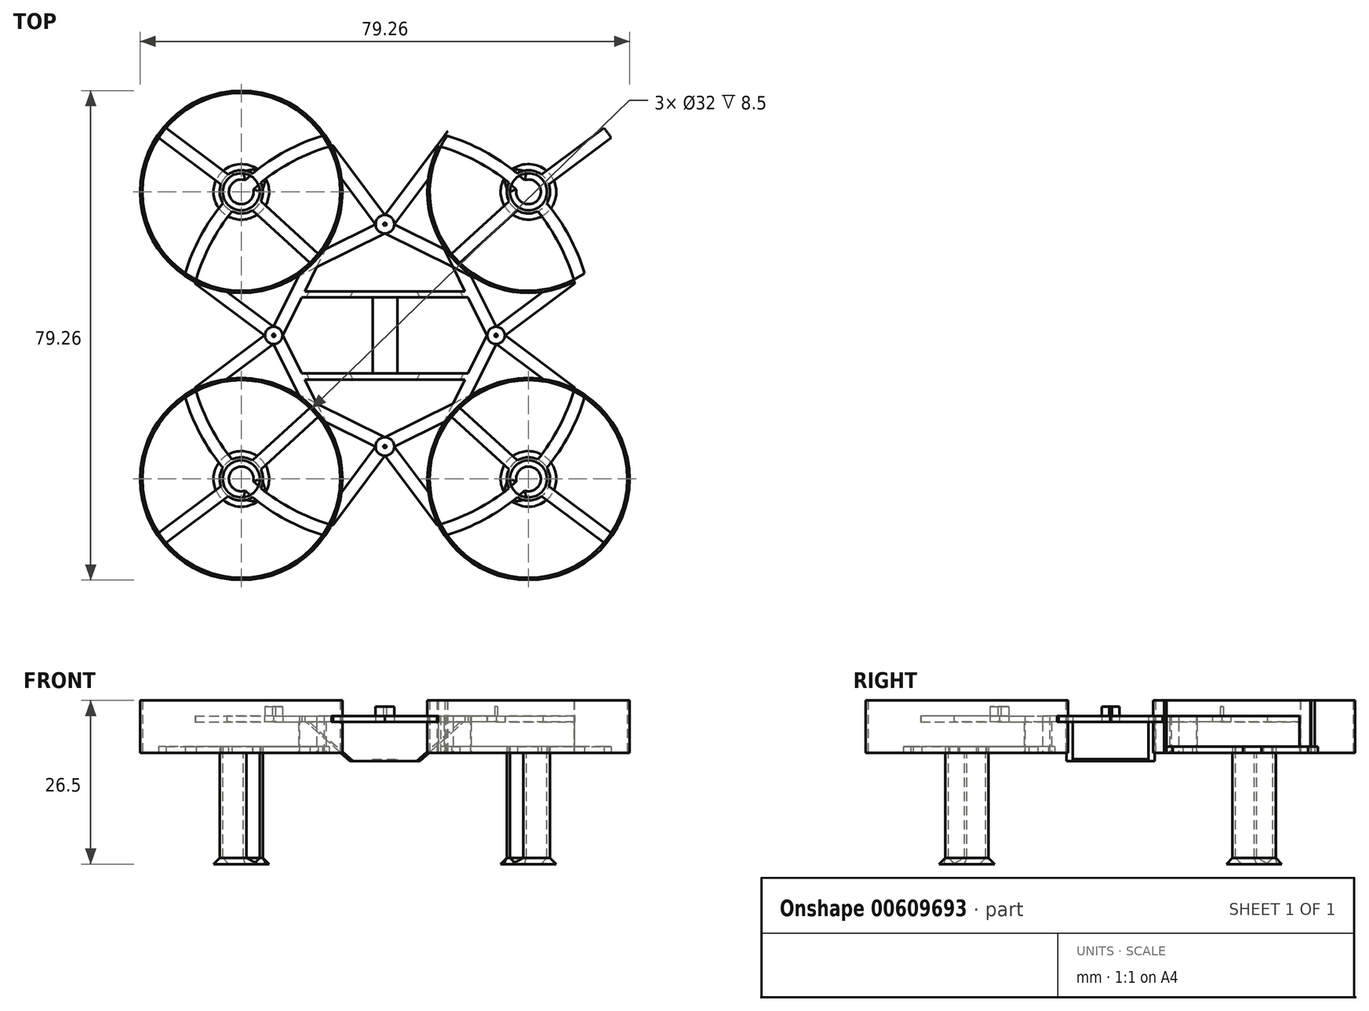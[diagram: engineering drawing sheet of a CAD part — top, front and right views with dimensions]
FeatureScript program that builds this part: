
annotation { "Feature Type Name" : "Feature", "Feature Type Description" : "" }
export const myFeature = defineFeature(function(context is Context, id is Id, definition is map)
    precondition{}
    {
        {
            var Q0;
            Q0=qCreatedBy(makeId("Top.planeOp"),FACE);
            var sketch = newSketch(context, id + "F0", { "sketchPlane" : qUnion([Q0])});
            skCircle(sketch, "E0", {"center": v(-23.25, 23.25) * mm, "radius": 16 * mm});
            skCircle(sketch, "E1", {"center": v(-23.25, -23.25) * mm, "radius": 16 * mm});
            skCircle(sketch, "E2", {"center": v(-18, 0) * mm, "radius": 0.25 * mm});
            skCircle(sketch, "E3", {"center": v(0, -18) * mm, "radius": 0.25 * mm});
            skCircle(sketch, "E4", {"center": v(-23.25, -23.25) * mm, "radius": 16.38 * mm});
            skCircle(sketch, "E5", {"center": v(-23.25, 23.25) * mm, "radius": 16.38 * mm});
            skCircle(sketch, "E6", {"center": v(-23.25, 23.25) * mm, "radius": 3.5 * mm});
            skCircle(sketch, "E7", {"center": v(-23.25, 23.25) * mm, "radius": 3 * mm});
            skCircle(sketch, "E8.0", {"center": v(0, 0) * mm, "radius": 33.88 * mm});
            skCircle(sketch, "E9.0", {"center": v(0, 0) * mm, "radius": 31.88 * mm});
            skCircle(sketch, "E10.MirrorC", {"center": v(-23.25, -23.25) * mm, "radius": 3.5 * mm});
            skCircle(sketch, "E11.MirrorC", {"center": v(-23.25, -23.25) * mm, "radius": 3 * mm});
            skLineSegment(sketch, "E12", {"start": v(-16.5, 0) * mm, "end": v(-8.58, -15.98) * mm});
            skLineSegment(sketch, "E13.MirrorCS", {"start": v(-16.5, 0) * mm, "end": v(-8.58, 15.98) * mm});
            skLineSegment(sketch, "E14", {"start": v(-33.06, -10.14) * mm, "end": v(-19.5, 0) * mm});
            skLineSegment(sketch, "E15", {"start": v(-18.04, -1.4) * mm, "end": v(-25.58, -7.04) * mm});
            skLineSegment(sketch, "E16.MirrorCS", {"start": v(-33.06, 10.14) * mm, "end": v(-19.5, 0) * mm});
            skLineSegment(sketch, "E17.MirrorCS", {"start": v(-18.04, 1.4) * mm, "end": v(-25.58, 7.04) * mm});
            skLineSegment(sketch, "E18.trimOffspring", {"start": v(-18.04, 1.4) * mm, "end": v(-13.85, 9.84) * mm});
            skLineSegment(sketch, "E19.trimOffspring", {"start": v(-18.04, -1.4) * mm, "end": v(-13.85, -9.84) * mm});
            skCircle(sketch, "E20.MirrorC", {"center": v(23.25, 23.25) * mm, "radius": 3 * mm});
            skCircle(sketch, "E21.MirrorC", {"center": v(23.25, 23.25) * mm, "radius": 3.5 * mm});
            skCircle(sketch, "E22.MirrorC", {"center": v(23.25, 23.25) * mm, "radius": 16 * mm});
            skCircle(sketch, "E23.MirrorC", {"center": v(23.25, 23.25) * mm, "radius": 16.38 * mm});
            skLineSegment(sketch, "E24.MirrorCS", {"start": v(16.5, 0) * mm, "end": v(8.58, 15.98) * mm});
            skLineSegment(sketch, "E25.MirrorCS", {"start": v(18.04, 1.4) * mm, "end": v(13.85, 9.84) * mm});
            skLineSegment(sketch, "E26.MirrorCS", {"start": v(18.04, 1.4) * mm, "end": v(25.58, 7.04) * mm});
            skLineSegment(sketch, "E27.MirrorCS", {"start": v(33.06, 10.14) * mm, "end": v(19.5, 0) * mm});
            skLineSegment(sketch, "E28.MirrorCS", {"start": v(33.06, -10.14) * mm, "end": v(19.5, 0) * mm});
            skLineSegment(sketch, "E29.MirrorCS", {"start": v(18.04, -1.4) * mm, "end": v(25.58, -7.04) * mm});
            skLineSegment(sketch, "E30.MirrorCS", {"start": v(18.04, -1.4) * mm, "end": v(13.85, -9.84) * mm});
            skLineSegment(sketch, "E31.MirrorCS", {"start": v(16.5, 0) * mm, "end": v(8.58, -15.98) * mm});
            skCircle(sketch, "E32.MirrorC", {"center": v(23.25, -23.25) * mm, "radius": 16.38 * mm});
            skCircle(sketch, "E33.MirrorC", {"center": v(23.25, -23.25) * mm, "radius": 16 * mm});
            skCircle(sketch, "E34.MirrorC", {"center": v(23.25, -23.25) * mm, "radius": 3 * mm});
            skCircle(sketch, "E35.MirrorC", {"center": v(23.25, -23.25) * mm, "radius": 3.5 * mm});
            skLineSegment(sketch, "E36", {"start": v(0, -16.5) * mm, "end": v(15.98, -8.58) * mm});
            skLineSegment(sketch, "E37", {"start": v(0, -16.5) * mm, "end": v(-15.98, -8.58) * mm});
            skLineSegment(sketch, "E38", {"start": v(-10.14, -33.06) * mm, "end": v(0, -19.5) * mm});
            skLineSegment(sketch, "E39", {"start": v(-1.5, -18) * mm, "end": v(-7.01, -25.37) * mm});
            skLineSegment(sketch, "E40", {"start": v(1.5, -18) * mm, "end": v(7.01, -25.37) * mm});
            skLineSegment(sketch, "E41.trimOffspring", {"start": v(-1.5, -18) * mm, "end": v(-9.83, -13.87) * mm});
            skLineSegment(sketch, "E42.trimOffspring", {"start": v(1.5, -18) * mm, "end": v(9.83, -13.87) * mm});
            skLineSegment(sketch, "E43", {"start": v(0, -19.5) * mm, "end": v(10.14, -33.06) * mm});
            skLineSegment(sketch, "E44.MirrorCS", {"start": v(0, 16.5) * mm, "end": v(15.98, 8.58) * mm});
            skLineSegment(sketch, "E45.MirrorCS", {"start": v(1.5, 18) * mm, "end": v(9.83, 13.87) * mm});
            skLineSegment(sketch, "E46.MirrorCS", {"start": v(1.5, 18) * mm, "end": v(7.01, 25.37) * mm});
            skLineSegment(sketch, "E47.MirrorCS", {"start": v(0, 19.5) * mm, "end": v(10.14, 33.06) * mm});
            skLineSegment(sketch, "E48.MirrorCS", {"start": v(-10.14, 33.06) * mm, "end": v(0, 19.5) * mm});
            skLineSegment(sketch, "E49.MirrorCS", {"start": v(-1.5, 18) * mm, "end": v(-7.01, 25.37) * mm});
            skLineSegment(sketch, "E50.MirrorCS", {"start": v(-1.5, 18) * mm, "end": v(-9.83, 13.87) * mm});
            skLineSegment(sketch, "E51.MirrorCS", {"start": v(0, 16.5) * mm, "end": v(-15.98, 8.58) * mm});
            skCircle(sketch, "E52.MirrorC", {"center": v(0, 18) * mm, "radius": 0.25 * mm});
            skLineSegment(sketch, "E53", {"start": v(-13.45, 6.15) * mm, "end": v(13.45, 6.15) * mm});
            skLineSegment(sketch, "E54", {"start": v(-13.45, -6.15) * mm, "end": v(13.45, -6.15) * mm});
            skLineSegment(sketch, "E55.0", {"start": v(-12.96, 7.15) * mm, "end": v(12.96, 7.15) * mm});
            skLineSegment(sketch, "E56.MirrorCS", {"start": v(-12.96, -7.15) * mm, "end": v(12.96, -7.15) * mm});
            skLineSegment(sketch, "E57", {"start": v(-2, 6.15) * mm, "end": v(-2, -6.15) * mm});
            skLineSegment(sketch, "E58.MirrorCS", {"start": v(2, 6.15) * mm, "end": v(2, -6.15) * mm});
            skLineSegment(sketch, "E59", {"start": v(-35.46, 33.58) * mm, "end": v(-25.34, 26.05) * mm});
            skLineSegment(sketch, "E60", {"start": v(-26.54, 24.45) * mm, "end": v(-36.66, 31.98) * mm});
            skLineSegment(sketch, "E61.MirrorCS", {"start": v(-26.54, -24.45) * mm, "end": v(-36.66, -31.98) * mm});
            skLineSegment(sketch, "E62.MirrorCS", {"start": v(-35.46, -33.58) * mm, "end": v(-25.34, -26.05) * mm});
            skLineSegment(sketch, "E63.MirrorCS", {"start": v(35.46, 33.58) * mm, "end": v(25.34, 26.05) * mm});
            skLineSegment(sketch, "E64.MirrorCS", {"start": v(26.54, 24.45) * mm, "end": v(36.66, 31.98) * mm});
            skLineSegment(sketch, "E65.MirrorCS", {"start": v(26.54, -24.45) * mm, "end": v(36.66, -31.98) * mm});
            skLineSegment(sketch, "E66.MirrorCS", {"start": v(35.46, -33.58) * mm, "end": v(25.34, -26.05) * mm});
            skLineSegment(sketch, "E67", {"start": v(20.1, 21.73) * mm, "end": v(10.78, 13.22) * mm});
            skLineSegment(sketch, "E68", {"start": v(21.45, 20.25) * mm, "end": v(12.13, 11.74) * mm});
            skLineSegment(sketch, "E69.MirrorCS", {"start": v(21.45, -20.25) * mm, "end": v(12.13, -11.74) * mm});
            skLineSegment(sketch, "E70.MirrorCS", {"start": v(20.1, -21.73) * mm, "end": v(10.78, -13.22) * mm});
            skLineSegment(sketch, "E71.MirrorCS", {"start": v(-20.1, 21.73) * mm, "end": v(-10.78, 13.22) * mm});
            skLineSegment(sketch, "E72.MirrorCS", {"start": v(-21.45, 20.25) * mm, "end": v(-12.13, 11.74) * mm});
            skLineSegment(sketch, "E73.MirrorCS", {"start": v(-21.45, -20.25) * mm, "end": v(-12.13, -11.74) * mm});
            skLineSegment(sketch, "E74.MirrorCS", {"start": v(-20.1, -21.73) * mm, "end": v(-10.78, -13.22) * mm});
            skCircle(sketch, "E75.MirrorC", {"center": v(18, 0) * mm, "radius": 0.25 * mm});
            skCircle(sketch, "E76", {"center": v(-18, 0) * mm, "radius": 1.4 * mm});
            skCircle(sketch, "E77", {"center": v(0, 18) * mm, "radius": 1.5 * mm});
            skCircle(sketch, "E78", {"center": v(18, 0) * mm, "radius": 1.4 * mm});
            skCircle(sketch, "E79", {"center": v(0, -18) * mm, "radius": 1.5 * mm});
            skLineSegment(sketch, "E80", {"start": v(-22.92, 26.23) * mm, "end": v(-22.44, 26.66) * mm});
            skLineSegment(sketch, "E81", {"start": v(-20.25, 23.25) * mm, "end": v(-19.78, 23.67) * mm});
            skLineSegment(sketch, "E82.MirrorCS", {"start": v(22.92, 26.23) * mm, "end": v(22.44, 26.66) * mm});
            skLineSegment(sketch, "E83.MirrorCS", {"start": v(20.25, 23.25) * mm, "end": v(19.78, 23.67) * mm});
            skLineSegment(sketch, "E84.MirrorCS", {"start": v(20.25, -23.25) * mm, "end": v(19.78, -23.67) * mm});
            skLineSegment(sketch, "E85.MirrorCS", {"start": v(22.92, -26.23) * mm, "end": v(22.44, -26.66) * mm});
            skLineSegment(sketch, "E86.MirrorCS", {"start": v(-20.25, -23.25) * mm, "end": v(-19.78, -23.67) * mm});
            skLineSegment(sketch, "E87.MirrorCS", {"start": v(-22.92, -26.23) * mm, "end": v(-22.44, -26.66) * mm});
            skSolve(sketch);
        }
        {
            var Q0;
            {var subQ0=sQuery(id+"F0.wireOp",EDGE,"E32.MirrorC");var subQ3=sQuery(id+"F0.wireOp",EDGE,"E8.0");var subQ5=makeQuery(id+"F0.imprint","INTERSECT",VERTEX,{"disambiguationData":[OD(0.0)],"derivedFrom":[subQ3,subQ0]});Q0=makeQuery(id+"F0.imprint","IMPRINT",FACE,{"disambiguationData":[TD([[makeQuery(id+"F0.imprint","IMPRINT",EDGE,{"disambiguationData":[TD([[subQ5,-1.0]])],"derivedFrom":subQ3}),-1.0]])]});}
            var Q1;
            {var subQ0=sQuery(id+"F0.wireOp",EDGE,"E32.MirrorC");var subQ1=sQuery(id+"F0.wireOp",EDGE,"E8.0");var subQ2=makeQuery(id+"F0.imprint","INTERSECT",VERTEX,{"disambiguationData":[OD(0.0)],"derivedFrom":[subQ1,subQ0]});Q1=makeQuery(id+"F0.imprint","IMPRINT",FACE,{"disambiguationData":[TD([[makeQuery(id+"F0.imprint","IMPRINT",EDGE,{"disambiguationData":[TD([[subQ2,-1.0]])],"derivedFrom":subQ1}),1.0]])]});}
            var Q2;
            {var subQ0=sQuery(id+"F0.wireOp",EDGE,"E32.MirrorC");var subQ2=sQuery(id+"F0.wireOp",EDGE,"E9.0");var subQ3=makeQuery(id+"F0.imprint","INTERSECT",VERTEX,{"disambiguationData":[OD(0.0)],"derivedFrom":[subQ2,subQ0]});Q2=makeQuery(id+"F0.imprint","IMPRINT",FACE,{"disambiguationData":[TD([[makeQuery(id+"F0.imprint","IMPRINT",EDGE,{"disambiguationData":[TD([[subQ3,-1.0]])],"derivedFrom":subQ2}),1.0]])]});}
            var Q3;
            {var subQ0=sQuery(id+"F0.wireOp",EDGE,"E33.MirrorC");var subQ1=sQuery(id+"F0.wireOp",EDGE,"E8.0");var subQ2=makeQuery(id+"F0.imprint","INTERSECT",VERTEX,{"disambiguationData":[OD(1.0)],"derivedFrom":[subQ1,subQ0]});Q3=makeQuery(id+"F0.imprint","IMPRINT",FACE,{"disambiguationData":[TD([[makeQuery(id+"F0.imprint","IMPRINT",EDGE,{"disambiguationData":[TD([[subQ2,-1.0]])],"derivedFrom":subQ1}),1.0]])]});}
            extrude(context, id + "F1", {"entities" : qUnion([Q0, Q1, Q2, Q3]), "depth" : 8.5 * mm, "offsetDistance" : 25 * mm});
        }
        {
            var Q0;
            {var subQ0=sQuery(id+"F0.wireOp",EDGE,"E23.MirrorC");var subQ4=sQuery(id+"F0.wireOp",EDGE,"E9.0");var subQ9=makeQuery(id+"F0.imprint","INTERSECT",VERTEX,{"disambiguationData":[OD(0.0)],"derivedFrom":[subQ4,subQ0]});Q0=makeQuery(id+"F0.imprint","IMPRINT",FACE,{"disambiguationData":[TD([[makeQuery(id+"F0.imprint","IMPRINT",EDGE,{"disambiguationData":[TD([[subQ9,-1.0]])],"derivedFrom":subQ4}),1.0]])]});}
            var Q1;
            {var subQ3=sQuery(id+"F0.wireOp",EDGE,"E8.0");var subQ5=sQuery(id+"F0.wireOp",EDGE,"E23.MirrorC");var subQ8=makeQuery(id+"F0.imprint","INTERSECT",VERTEX,{"disambiguationData":[OD(0.0)],"derivedFrom":[subQ3,subQ5]});Q1=makeQuery(id+"F0.imprint","IMPRINT",FACE,{"disambiguationData":[TD([[makeQuery(id+"F0.imprint","IMPRINT",EDGE,{"disambiguationData":[TD([[subQ8,-1.0]])],"derivedFrom":subQ3}),-1.0]])]});}
            var Q2;
            {var subQ0=sQuery(id+"F0.wireOp",EDGE,"E22.MirrorC");var subQ1=sQuery(id+"F0.wireOp",EDGE,"E8.0");var subQ2=makeQuery(id+"F0.imprint","INTERSECT",VERTEX,{"disambiguationData":[OD(1.0)],"derivedFrom":[subQ1,subQ0]});Q2=makeQuery(id+"F0.imprint","IMPRINT",FACE,{"disambiguationData":[TD([[makeQuery(id+"F0.imprint","IMPRINT",EDGE,{"disambiguationData":[TD([[subQ2,-1.0]])],"derivedFrom":subQ1}),1.0]])]});}
            var Q3;
            {var subQ0=sQuery(id+"F0.wireOp",EDGE,"E23.MirrorC");var subQ1=sQuery(id+"F0.wireOp",EDGE,"E8.0");var subQ2=makeQuery(id+"F0.imprint","INTERSECT",VERTEX,{"disambiguationData":[OD(0.0)],"derivedFrom":[subQ1,subQ0]});Q3=makeQuery(id+"F0.imprint","IMPRINT",FACE,{"disambiguationData":[TD([[makeQuery(id+"F0.imprint","IMPRINT",EDGE,{"disambiguationData":[TD([[subQ2,-1.0]])],"derivedFrom":subQ1}),1.0]])]});}
            var Q4;
            {var subQ5=sQuery(id+"F0.wireOp",EDGE,"E0");var subQ9=makeQuery(id+"F0.imprint","INTERSECT",VERTEX,{"derivedFrom":[subQ5,sQuery(id+"F0.wireOp",EDGE,"E72.MirrorCS")]});Q4=makeQuery(id+"F0.imprint","IMPRINT",FACE,{"disambiguationData":[TD([[makeQuery(id+"F0.imprint","IMPRINT",EDGE,{"disambiguationData":[TD([[subQ9,1.0]])],"derivedFrom":subQ5}),-1.0]])]});}
            var Q5;
            {var subQ0=sQuery(id+"F0.wireOp",EDGE,"E8.0");var subQ1=sQuery(id+"F0.wireOp",EDGE,"E0");var subQ2=makeQuery(id+"F0.imprint","INTERSECT",VERTEX,{"disambiguationData":[OD(0.0)],"derivedFrom":[subQ1,subQ0]});Q5=makeQuery(id+"F0.imprint","IMPRINT",FACE,{"disambiguationData":[TD([[makeQuery(id+"F0.imprint","IMPRINT",EDGE,{"disambiguationData":[TD([[subQ2,1.0]])],"derivedFrom":subQ1}),-1.0]])]});}
            var Q6;
            {var subQ0=sQuery(id+"F0.wireOp",EDGE,"E0");var subQ8=makeQuery(id+"F0.imprint","INTERSECT",VERTEX,{"derivedFrom":[subQ0,sQuery(id+"F0.wireOp",EDGE,"E59")]});Q6=makeQuery(id+"F0.imprint","IMPRINT",FACE,{"disambiguationData":[TD([[makeQuery(id+"F0.imprint","IMPRINT",EDGE,{"disambiguationData":[TD([[subQ8,1.0]])],"derivedFrom":subQ0}),-1.0]])]});}
            var Q7;
            {var subQ0=sQuery(id+"F0.wireOp",EDGE,"E8.0");var subQ1=sQuery(id+"F0.wireOp",EDGE,"E0");var subQ2=makeQuery(id+"F0.imprint","INTERSECT",VERTEX,{"disambiguationData":[OD(1.0)],"derivedFrom":[subQ1,subQ0]});Q7=makeQuery(id+"F0.imprint","IMPRINT",FACE,{"disambiguationData":[TD([[makeQuery(id+"F0.imprint","IMPRINT",EDGE,{"disambiguationData":[TD([[subQ2,-1.0]])],"derivedFrom":subQ1}),-1.0]])]});}
            var Q8;
            {var subQ4=sQuery(id+"F0.wireOp",EDGE,"E1");var subQ7=makeQuery(id+"F0.imprint","INTERSECT",VERTEX,{"derivedFrom":[subQ4,sQuery(id+"F0.wireOp",EDGE,"E61.MirrorCS")]});Q8=makeQuery(id+"F0.imprint","IMPRINT",FACE,{"disambiguationData":[TD([[makeQuery(id+"F0.imprint","IMPRINT",EDGE,{"disambiguationData":[TD([[subQ7,1.0]])],"derivedFrom":subQ4}),-1.0]])]});}
            var Q9;
            {var subQ0=sQuery(id+"F0.wireOp",EDGE,"E8.0");var subQ1=sQuery(id+"F0.wireOp",EDGE,"E1");var subQ2=makeQuery(id+"F0.imprint","INTERSECT",VERTEX,{"disambiguationData":[OD(1.0)],"derivedFrom":[subQ1,subQ0]});Q9=makeQuery(id+"F0.imprint","IMPRINT",FACE,{"disambiguationData":[TD([[makeQuery(id+"F0.imprint","IMPRINT",EDGE,{"disambiguationData":[TD([[subQ2,-1.0]])],"derivedFrom":subQ1}),-1.0]])]});}
            var Q10;
            {var subQ9=sQuery(id+"F0.wireOp",EDGE,"E1");var subQ10=makeQuery(id+"F0.imprint","INTERSECT",VERTEX,{"derivedFrom":[subQ9,sQuery(id+"F0.wireOp",EDGE,"E73.MirrorCS")]});Q10=makeQuery(id+"F0.imprint","IMPRINT",FACE,{"disambiguationData":[TD([[makeQuery(id+"F0.imprint","IMPRINT",EDGE,{"disambiguationData":[TD([[subQ10,1.0]])],"derivedFrom":subQ9}),-1.0]])]});}
            var Q11;
            {var subQ0=sQuery(id+"F0.wireOp",EDGE,"E9.0");var subQ1=sQuery(id+"F0.wireOp",EDGE,"E1");var subQ2=makeQuery(id+"F0.imprint","INTERSECT",VERTEX,{"disambiguationData":[OD(0.0)],"derivedFrom":[subQ1,subQ0]});Q11=makeQuery(id+"F0.imprint","IMPRINT",FACE,{"disambiguationData":[TD([[makeQuery(id+"F0.imprint","IMPRINT",EDGE,{"disambiguationData":[TD([[subQ2,-1.0]])],"derivedFrom":subQ1}),-1.0]])]});}
            extrude(context, id + "F2", {"entities" : qUnion([Q0, Q1, Q2, Q3, Q4, Q5, Q6, Q7, Q8, Q9, Q10, Q11]), "depth" : 8.5 * mm, "offsetDistance" : 25 * mm});
        }
        {
            var Q0;
            {var subQ0=sQuery(id+"F0.wireOp",EDGE,"E46.MirrorCS");Q0=makeQuery(id+"F0.imprint","IMPRINT",FACE,{"disambiguationData":[TD([[makeQuery(id+"F0.imprint","IMPRINT",EDGE,{"derivedFrom":subQ0}),1.0]])]});}
            var Q1;
            {var subQ5=sQuery(id+"F0.wireOp",EDGE,"E26.MirrorCS");Q1=makeQuery(id+"F0.imprint","IMPRINT",FACE,{"disambiguationData":[TD([[makeQuery(id+"F0.imprint","IMPRINT",EDGE,{"derivedFrom":subQ5}),-1.0]])]});}
            var Q2;
            Q2=makeQuery(id+"F0.imprint","IMPRINT",FACE,{"disambiguationData":[TD([[makeQuery(id+"F0.imprint","IMPRINT",EDGE,{"derivedFrom":sQuery(id+"F0.wireOp",EDGE,"E3")}),-1.0]])]});
            var Q3;
            Q3=makeQuery(id+"F0.imprint","IMPRINT",FACE,{"disambiguationData":[TD([[makeQuery(id+"F0.imprint","IMPRINT",EDGE,{"derivedFrom":sQuery(id+"F0.wireOp",EDGE,"E2")}),-1.0]])]});
            var Q4;
            {var subQ3=sQuery(id+"F0.wireOp",EDGE,"E19.trimOffspring");var subQ5=sQuery(id+"F0.wireOp",EDGE,"E4");var subQ6=makeQuery(id+"F0.imprint","INTERSECT",VERTEX,{"derivedFrom":[subQ5,subQ3]});Q4=makeQuery(id+"F0.imprint","IMPRINT",FACE,{"disambiguationData":[TD([[makeQuery(id+"F0.imprint","IMPRINT",EDGE,{"disambiguationData":[TD([[subQ6,1.0]])],"derivedFrom":subQ5}),-1.0]])]});}
            var Q5;
            {var subQ0=sQuery(id+"F0.wireOp",EDGE,"E32.MirrorC");var subQ1=sQuery(id+"F0.wireOp",EDGE,"E30.MirrorCS");var subQ2=makeQuery(id+"F0.imprint","INTERSECT",VERTEX,{"derivedFrom":[subQ1,subQ0]});Q5=makeQuery(id+"F0.imprint","IMPRINT",FACE,{"disambiguationData":[TD([[makeQuery(id+"F0.imprint","IMPRINT",EDGE,{"disambiguationData":[TD([[subQ2,1.0]])],"derivedFrom":subQ1}),-1.0]])]});}
            var Q6;
            {var subQ0=sQuery(id+"F0.wireOp",EDGE,"E25.MirrorCS");var subQ1=sQuery(id+"F0.wireOp",EDGE,"E23.MirrorC");var subQ2=makeQuery(id+"F0.imprint","INTERSECT",VERTEX,{"derivedFrom":[subQ1,subQ0]});Q6=makeQuery(id+"F0.imprint","IMPRINT",FACE,{"disambiguationData":[TD([[makeQuery(id+"F0.imprint","IMPRINT",EDGE,{"disambiguationData":[TD([[subQ2,-1.0]])],"derivedFrom":subQ1}),1.0]])]});}
            var Q7;
            {var subQ1=sQuery(id+"F0.wireOp",EDGE,"E5");var subQ5=sQuery(id+"F0.wireOp",EDGE,"E18.trimOffspring");var subQ6=makeQuery(id+"F0.imprint","INTERSECT",VERTEX,{"derivedFrom":[subQ1,subQ5]});Q7=makeQuery(id+"F0.imprint","IMPRINT",FACE,{"disambiguationData":[TD([[makeQuery(id+"F0.imprint","IMPRINT",EDGE,{"disambiguationData":[TD([[subQ6,-1.0]])],"derivedFrom":subQ1}),-1.0]])]});}
            var Q8;
            {var subQ5=sQuery(id+"F0.wireOp",EDGE,"E56.MirrorCS");Q8=makeQuery(id+"F0.imprint","IMPRINT",FACE,{"disambiguationData":[TD([[makeQuery(id+"F0.imprint","IMPRINT",EDGE,{"derivedFrom":subQ5}),1.0]])]});}
            var Q9;
            {var subQ6=sQuery(id+"F0.wireOp",EDGE,"E55.0");Q9=makeQuery(id+"F0.imprint","IMPRINT",FACE,{"disambiguationData":[TD([[makeQuery(id+"F0.imprint","IMPRINT",EDGE,{"derivedFrom":subQ6}),-1.0]])]});}
            var Q10;
            {var subQ1=sQuery(id+"F0.wireOp",EDGE,"E13.MirrorCS");var subQ10=sQuery(id+"F0.wireOp",EDGE,"E12");var subQ15=makeQuery(id+"F0.imprint","INTERSECT",VERTEX,{"derivedFrom":[subQ10,subQ1]});Q10=makeQuery(id+"F0.imprint","IMPRINT",FACE,{"disambiguationData":[TD([[makeQuery(id+"F0.imprint","IMPRINT",EDGE,{"disambiguationData":[TD([[subQ15,-1.0]])],"derivedFrom":subQ10}),-1.0]])]});}
            var Q11;
            {var subQ11=sQuery(id+"F0.wireOp",EDGE,"E15");Q11=makeQuery(id+"F0.imprint","IMPRINT",FACE,{"disambiguationData":[TD([[makeQuery(id+"F0.imprint","IMPRINT",EDGE,{"derivedFrom":subQ11}),-1.0]])]});}
            var Q12;
            {var subQ0=sQuery(id+"F0.wireOp",EDGE,"E37");var subQ1=sQuery(id+"F0.wireOp",EDGE,"E12");var subQ2=makeQuery(id+"F0.imprint","INTERSECT",VERTEX,{"derivedFrom":[subQ1,subQ0]});Q12=makeQuery(id+"F0.imprint","IMPRINT",FACE,{"disambiguationData":[TD([[makeQuery(id+"F0.imprint","IMPRINT",EDGE,{"disambiguationData":[TD([[subQ2,-1.0]])],"derivedFrom":subQ1}),1.0]])]});}
            var Q13;
            {var subQ5=sQuery(id+"F0.wireOp",EDGE,"E39");Q13=makeQuery(id+"F0.imprint","IMPRINT",FACE,{"disambiguationData":[TD([[makeQuery(id+"F0.imprint","IMPRINT",EDGE,{"derivedFrom":subQ5}),1.0]])]});}
            var Q14;
            {var subQ0=sQuery(id+"F0.wireOp",EDGE,"E40");Q14=makeQuery(id+"F0.imprint","IMPRINT",FACE,{"disambiguationData":[TD([[makeQuery(id+"F0.imprint","IMPRINT",EDGE,{"derivedFrom":subQ0}),-1.0]])]});}
            var Q15;
            {var subQ0=sQuery(id+"F0.wireOp",EDGE,"E36");var subQ1=sQuery(id+"F0.wireOp",EDGE,"E31.MirrorCS");var subQ2=makeQuery(id+"F0.imprint","INTERSECT",VERTEX,{"derivedFrom":[subQ1,subQ0]});Q15=makeQuery(id+"F0.imprint","IMPRINT",FACE,{"disambiguationData":[TD([[makeQuery(id+"F0.imprint","IMPRINT",EDGE,{"disambiguationData":[TD([[subQ2,-1.0]])],"derivedFrom":subQ1}),-1.0]])]});}
            var Q16;
            Q16=makeQuery(id+"F0.imprint","IMPRINT",FACE,{"disambiguationData":[TD([[makeQuery(id+"F0.imprint","IMPRINT",EDGE,{"derivedFrom":sQuery(id+"F0.wireOp",EDGE,"E75.MirrorC")}),1.0]])]});
            var Q17;
            {var subQ0=sQuery(id+"F0.wireOp",EDGE,"E31.MirrorCS");var subQ5=sQuery(id+"F0.wireOp",EDGE,"E24.MirrorCS");var subQ10=makeQuery(id+"F0.imprint","INTERSECT",VERTEX,{"derivedFrom":[subQ5,subQ0]});Q17=makeQuery(id+"F0.imprint","IMPRINT",FACE,{"disambiguationData":[TD([[makeQuery(id+"F0.imprint","IMPRINT",EDGE,{"disambiguationData":[TD([[subQ10,-1.0]])],"derivedFrom":subQ5}),-1.0]])]});}
            var Q18;
            {var subQ5=sQuery(id+"F0.wireOp",EDGE,"E49.MirrorCS");Q18=makeQuery(id+"F0.imprint","IMPRINT",FACE,{"disambiguationData":[TD([[makeQuery(id+"F0.imprint","IMPRINT",EDGE,{"derivedFrom":subQ5}),-1.0]])]});}
            var Q19;
            {var subQ0=sQuery(id+"F0.wireOp",EDGE,"E51.MirrorCS");var subQ1=sQuery(id+"F0.wireOp",EDGE,"E13.MirrorCS");var subQ2=makeQuery(id+"F0.imprint","INTERSECT",VERTEX,{"derivedFrom":[subQ1,subQ0]});Q19=makeQuery(id+"F0.imprint","IMPRINT",FACE,{"disambiguationData":[TD([[makeQuery(id+"F0.imprint","IMPRINT",EDGE,{"disambiguationData":[TD([[subQ2,-1.0]])],"derivedFrom":subQ1}),-1.0]])]});}
            var Q20;
            {var subQ0=sQuery(id+"F0.wireOp",EDGE,"E44.MirrorCS");var subQ1=sQuery(id+"F0.wireOp",EDGE,"E24.MirrorCS");var subQ2=makeQuery(id+"F0.imprint","INTERSECT",VERTEX,{"derivedFrom":[subQ1,subQ0]});Q20=makeQuery(id+"F0.imprint","IMPRINT",FACE,{"disambiguationData":[TD([[makeQuery(id+"F0.imprint","IMPRINT",EDGE,{"disambiguationData":[TD([[subQ2,-1.0]])],"derivedFrom":subQ1}),1.0]])]});}
            var Q21;
            Q21=makeQuery(id+"F0.imprint","IMPRINT",FACE,{"disambiguationData":[TD([[makeQuery(id+"F0.imprint","IMPRINT",EDGE,{"derivedFrom":sQuery(id+"F0.wireOp",EDGE,"E52.MirrorC")}),1.0]])]});
            extrude(context, id + "F3", {"entities" : qUnion([Q0, Q1, Q2, Q3, Q4, Q5, Q6, Q7, Q8, Q9, Q10, Q11, Q12, Q13, Q14, Q15, Q16, Q17, Q18, Q19, Q20, Q21]), "depth" : 6 * mm, "offsetDistance" : 25 * mm});
        }
        {
            var Q0;
            {var subQ1=sQuery(id+"F0.wireOp",EDGE,"E9.0");var subQ4=sQuery(id+"F0.wireOp",EDGE,"E21.MirrorC");var subQ7=makeQuery(id+"F0.imprint","INTERSECT",VERTEX,{"disambiguationData":[OD(0.0)],"derivedFrom":[subQ1,subQ4]});Q0=makeQuery(id+"F0.imprint","IMPRINT",FACE,{"disambiguationData":[TD([[makeQuery(id+"F0.imprint","IMPRINT",EDGE,{"disambiguationData":[TD([[subQ7,-1.0]])],"derivedFrom":subQ1}),1.0]])]});}
            var Q1;
            {var subQ0=sQuery(id+"F0.wireOp",EDGE,"E21.MirrorC");var subQ2=sQuery(id+"F0.wireOp",EDGE,"E8.0");var subQ7=makeQuery(id+"F0.imprint","INTERSECT",VERTEX,{"disambiguationData":[OD(0.0)],"derivedFrom":[subQ2,subQ0]});Q1=makeQuery(id+"F0.imprint","IMPRINT",FACE,{"disambiguationData":[TD([[makeQuery(id+"F0.imprint","IMPRINT",EDGE,{"disambiguationData":[TD([[subQ7,-1.0]])],"derivedFrom":subQ2}),-1.0]])]});}
            var Q2;
            {var subQ0=sQuery(id+"F0.wireOp",EDGE,"E10.MirrorC");var subQ3=sQuery(id+"F0.wireOp",EDGE,"E9.0");var subQ4=makeQuery(id+"F0.imprint","INTERSECT",VERTEX,{"disambiguationData":[OD(0.0)],"derivedFrom":[subQ3,subQ0]});Q2=makeQuery(id+"F0.imprint","IMPRINT",FACE,{"disambiguationData":[TD([[makeQuery(id+"F0.imprint","IMPRINT",EDGE,{"disambiguationData":[TD([[subQ4,-1.0]])],"derivedFrom":subQ3}),1.0]])]});}
            var Q3;
            {var subQ0=sQuery(id+"F0.wireOp",EDGE,"E10.MirrorC");var subQ3=sQuery(id+"F0.wireOp",EDGE,"E8.0");var subQ7=makeQuery(id+"F0.imprint","INTERSECT",VERTEX,{"disambiguationData":[OD(0.0)],"derivedFrom":[subQ3,subQ0]});Q3=makeQuery(id+"F0.imprint","IMPRINT",FACE,{"disambiguationData":[TD([[makeQuery(id+"F0.imprint","IMPRINT",EDGE,{"disambiguationData":[TD([[subQ7,-1.0]])],"derivedFrom":subQ3}),-1.0]])]});}
            var Q4;
            {var subQ4=sQuery(id+"F0.wireOp",EDGE,"E6");var subQ8=makeQuery(id+"F0.imprint","INTERSECT",VERTEX,{"derivedFrom":[subQ4,sQuery(id+"F0.wireOp",EDGE,"E59")]});Q4=makeQuery(id+"F0.imprint","IMPRINT",FACE,{"disambiguationData":[TD([[makeQuery(id+"F0.imprint","IMPRINT",EDGE,{"disambiguationData":[TD([[subQ8,1.0]])],"derivedFrom":subQ4}),1.0]])]});}
            var Q5;
            {var subQ0=sQuery(id+"F0.wireOp",EDGE,"E6");var subQ7=makeQuery(id+"F0.imprint","INTERSECT",VERTEX,{"derivedFrom":[subQ0,sQuery(id+"F0.wireOp",EDGE,"E72.MirrorCS")]});Q5=makeQuery(id+"F0.imprint","IMPRINT",FACE,{"disambiguationData":[TD([[makeQuery(id+"F0.imprint","IMPRINT",EDGE,{"disambiguationData":[TD([[subQ7,1.0]])],"derivedFrom":subQ0}),1.0]])]});}
            var Q6;
            {var subQ0=sQuery(id+"F0.wireOp",EDGE,"E8.0");var subQ1=sQuery(id+"F0.wireOp",EDGE,"E6");var subQ2=makeQuery(id+"F0.imprint","INTERSECT",VERTEX,{"disambiguationData":[OD(1.0)],"derivedFrom":[subQ1,subQ0]});Q6=makeQuery(id+"F0.imprint","IMPRINT",FACE,{"disambiguationData":[TD([[makeQuery(id+"F0.imprint","IMPRINT",EDGE,{"disambiguationData":[TD([[subQ2,-1.0]])],"derivedFrom":subQ1}),1.0]])]});}
            var Q7;
            {var subQ0=sQuery(id+"F0.wireOp",EDGE,"E10.MirrorC");var subQ1=sQuery(id+"F0.wireOp",EDGE,"E8.0");var subQ2=makeQuery(id+"F0.imprint","INTERSECT",VERTEX,{"disambiguationData":[OD(0.0)],"derivedFrom":[subQ1,subQ0]});Q7=makeQuery(id+"F0.imprint","IMPRINT",FACE,{"disambiguationData":[TD([[makeQuery(id+"F0.imprint","IMPRINT",EDGE,{"disambiguationData":[TD([[subQ2,-1.0]])],"derivedFrom":subQ1}),1.0]])]});}
            var Q8;
            {var subQ4=sQuery(id+"F0.wireOp",EDGE,"E84.MirrorCS");Q8=makeQuery(id+"F0.imprint","IMPRINT",FACE,{"disambiguationData":[TD([[makeQuery(id+"F0.imprint","IMPRINT",EDGE,{"derivedFrom":subQ4}),-1.0]])]});}
            var Q9;
            {var subQ0=sQuery(id+"F0.wireOp",EDGE,"E34.MirrorC");var subQ1=sQuery(id+"F0.wireOp",EDGE,"E8.0");var subQ2=makeQuery(id+"F0.imprint","INTERSECT",VERTEX,{"disambiguationData":[OD(1.0)],"derivedFrom":[subQ1,subQ0]});Q9=makeQuery(id+"F0.imprint","IMPRINT",FACE,{"disambiguationData":[TD([[makeQuery(id+"F0.imprint","IMPRINT",EDGE,{"disambiguationData":[TD([[subQ2,-1.0]])],"derivedFrom":subQ1}),1.0]])]});}
            var Q10;
            {var subQ3=sQuery(id+"F0.wireOp",EDGE,"E85.MirrorCS");Q10=makeQuery(id+"F0.imprint","IMPRINT",FACE,{"disambiguationData":[TD([[makeQuery(id+"F0.imprint","IMPRINT",EDGE,{"derivedFrom":subQ3}),1.0]])]});}
            var Q11;
            {var subQ0=sQuery(id+"F0.wireOp",EDGE,"E21.MirrorC");var subQ1=sQuery(id+"F0.wireOp",EDGE,"E8.0");var subQ2=makeQuery(id+"F0.imprint","INTERSECT",VERTEX,{"disambiguationData":[OD(0.0)],"derivedFrom":[subQ1,subQ0]});Q11=makeQuery(id+"F0.imprint","IMPRINT",FACE,{"disambiguationData":[TD([[makeQuery(id+"F0.imprint","IMPRINT",EDGE,{"disambiguationData":[TD([[subQ2,-1.0]])],"derivedFrom":subQ1}),1.0]])]});}
            extrude(context, id + "F4", {"entities" : qUnion([Q0, Q1, Q2, Q3, Q4, Q5, Q6, Q7, Q8, Q9, Q10, Q11]), "oppositeDirection" : true, "depth" : 17 * mm, "offsetDistance" : 25 * mm});
        }
        {
            var Q0;
            Q0=makeQuery(id+"F4.opExtrude","CAP_FACE",FACE,{"disambiguationData":[OSD([sQuery(id+"F0.wireOp",EDGE,"E10.MirrorC"),sQuery(id+"F0.wireOp",EDGE,"E11.MirrorC")])],"isStart":false});
            var Q1;
            Q1=makeQuery(id+"F4.opExtrude","CAP_FACE",FACE,{"disambiguationData":[OSD([sQuery(id+"F0.wireOp",EDGE,"E6"),sQuery(id+"F0.wireOp",EDGE,"E7")])],"isStart":false});
            var Q2;
            Q2=makeQuery(id+"F4.opExtrude","CAP_FACE",FACE,{"disambiguationData":[OSD([sQuery(id+"F0.wireOp",EDGE,"E34.MirrorC"),sQuery(id+"F0.wireOp",EDGE,"E35.MirrorC")])],"isStart":false});
            var Q3;
            Q3=makeQuery(id+"F4.opExtrude","CAP_FACE",FACE,{"disambiguationData":[OSD([sQuery(id+"F0.wireOp",EDGE,"E20.MirrorC"),sQuery(id+"F0.wireOp",EDGE,"E21.MirrorC")])],"isStart":false});
            extrude(context, id + "F5", {"entities" : qUnion([Q0, Q1, Q2, Q3]), "depth" : 1 * mm, "offsetDistance" : 25 * mm, "hasDraft" : true, "draftAngle" : 45 * degree});
        }
        {
            var Q0;
            {var subQ6=sQuery(id+"F0.wireOp",EDGE,"E55.0");Q0=makeQuery(id+"F0.imprint","IMPRINT",FACE,{"disambiguationData":[TD([[makeQuery(id+"F0.imprint","IMPRINT",EDGE,{"derivedFrom":subQ6}),-1.0]])]});}
            var Q1;
            {var subQ5=sQuery(id+"F0.wireOp",EDGE,"E56.MirrorCS");Q1=makeQuery(id+"F0.imprint","IMPRINT",FACE,{"disambiguationData":[TD([[makeQuery(id+"F0.imprint","IMPRINT",EDGE,{"derivedFrom":subQ5}),1.0]])]});}
            var Q2;
            {var subQ0=sQuery(id+"F0.wireOp",EDGE,"E57");Q2=makeQuery(id+"F0.imprint","IMPRINT",FACE,{"disambiguationData":[TD([[makeQuery(id+"F0.imprint","IMPRINT",EDGE,{"derivedFrom":subQ0}),1.0]])]});}
            extrude(context, id + "F6", {"entities" : qUnion([Q0, Q1, Q2]), "operationType" : NewBodyOperationType.ADD, "oppositeDirection" : true, "depth" : 1.35 * mm, "offsetDistance" : 25 * mm});
        }
        {
            var Q0;
            {var subQ0=sQuery(id+"F0.wireOp",EDGE,"E57");Q0=makeQuery(id+"F0.imprint","IMPRINT",FACE,{"disambiguationData":[TD([[makeQuery(id+"F0.imprint","IMPRINT",EDGE,{"derivedFrom":subQ0}),1.0]])]});}
            extrude(context, id + "F7", {"entities" : qUnion([Q0]), "operationType" : NewBodyOperationType.REMOVE, "oppositeDirection" : true, "depth" : 1 * mm, "offsetDistance" : 25 * mm});
        }
        {
            var Q0;
            Q0=makeQuery(id+"F0.imprint","IMPRINT",FACE,{"disambiguationData":[TD([[makeQuery(id+"F0.imprint","IMPRINT",EDGE,{"derivedFrom":sQuery(id+"F0.wireOp",EDGE,"E75.MirrorC")}),1.0]])]});
            var Q1;
            Q1=makeQuery(id+"F0.imprint","IMPRINT",FACE,{"disambiguationData":[TD([[makeQuery(id+"F0.imprint","IMPRINT",EDGE,{"derivedFrom":sQuery(id+"F0.wireOp",EDGE,"E52.MirrorC")}),1.0]])]});
            var Q2;
            Q2=makeQuery(id+"F0.imprint","IMPRINT",FACE,{"disambiguationData":[TD([[makeQuery(id+"F0.imprint","IMPRINT",EDGE,{"derivedFrom":sQuery(id+"F0.wireOp",EDGE,"E2")}),-1.0]])]});
            var Q3;
            Q3=makeQuery(id+"F0.imprint","IMPRINT",FACE,{"disambiguationData":[TD([[makeQuery(id+"F0.imprint","IMPRINT",EDGE,{"derivedFrom":sQuery(id+"F0.wireOp",EDGE,"E3")}),-1.0]])]});
            extrude(context, id + "F8", {"entities" : qUnion([Q0, Q1, Q2, Q3]), "operationType" : NewBodyOperationType.ADD, "depth" : 7.5 * mm, "offsetDistance" : 25 * mm});
        }
        {
            var Q0;
            {var subQ5=sQuery(id+"F0.wireOp",EDGE,"E39");Q0=makeQuery(id+"F0.imprint","IMPRINT",FACE,{"disambiguationData":[TD([[makeQuery(id+"F0.imprint","IMPRINT",EDGE,{"derivedFrom":subQ5}),1.0]])]});}
            var Q1;
            {var subQ0=sQuery(id+"F0.wireOp",EDGE,"E40");Q1=makeQuery(id+"F0.imprint","IMPRINT",FACE,{"disambiguationData":[TD([[makeQuery(id+"F0.imprint","IMPRINT",EDGE,{"derivedFrom":subQ0}),-1.0]])]});}
            var Q2;
            {var subQ0=sQuery(id+"F0.wireOp",EDGE,"E36");var subQ1=sQuery(id+"F0.wireOp",EDGE,"E31.MirrorCS");var subQ2=makeQuery(id+"F0.imprint","INTERSECT",VERTEX,{"derivedFrom":[subQ1,subQ0]});Q2=makeQuery(id+"F0.imprint","IMPRINT",FACE,{"disambiguationData":[TD([[makeQuery(id+"F0.imprint","IMPRINT",EDGE,{"disambiguationData":[TD([[subQ2,-1.0]])],"derivedFrom":subQ1}),-1.0]])]});}
            var Q3;
            Q3=makeQuery(id+"F0.imprint","IMPRINT",FACE,{"disambiguationData":[TD([[makeQuery(id+"F0.imprint","IMPRINT",EDGE,{"derivedFrom":sQuery(id+"F0.wireOp",EDGE,"E3")}),-1.0]])]});
            var Q4;
            {var subQ0=sQuery(id+"F0.wireOp",EDGE,"E37");var subQ1=sQuery(id+"F0.wireOp",EDGE,"E12");var subQ2=makeQuery(id+"F0.imprint","INTERSECT",VERTEX,{"derivedFrom":[subQ1,subQ0]});Q4=makeQuery(id+"F0.imprint","IMPRINT",FACE,{"disambiguationData":[TD([[makeQuery(id+"F0.imprint","IMPRINT",EDGE,{"disambiguationData":[TD([[subQ2,-1.0]])],"derivedFrom":subQ1}),1.0]])]});}
            var Q5;
            {var subQ0=sQuery(id+"F0.wireOp",EDGE,"E31.MirrorCS");var subQ5=sQuery(id+"F0.wireOp",EDGE,"E24.MirrorCS");var subQ10=makeQuery(id+"F0.imprint","INTERSECT",VERTEX,{"derivedFrom":[subQ5,subQ0]});Q5=makeQuery(id+"F0.imprint","IMPRINT",FACE,{"disambiguationData":[TD([[makeQuery(id+"F0.imprint","IMPRINT",EDGE,{"disambiguationData":[TD([[subQ10,-1.0]])],"derivedFrom":subQ5}),-1.0]])]});}
            var Q6;
            {var subQ0=sQuery(id+"F0.wireOp",EDGE,"E26.MirrorCS");Q6=makeQuery(id+"F0.imprint","IMPRINT",FACE,{"disambiguationData":[TD([[makeQuery(id+"F0.imprint","IMPRINT",EDGE,{"derivedFrom":subQ0}),-1.0]])]});}
            var Q7;
            Q7=makeQuery(id+"F0.imprint","IMPRINT",FACE,{"disambiguationData":[TD([[makeQuery(id+"F0.imprint","IMPRINT",EDGE,{"derivedFrom":sQuery(id+"F0.wireOp",EDGE,"E75.MirrorC")}),1.0]])]});
            var Q8;
            {var subQ0=sQuery(id+"F0.wireOp",EDGE,"E51.MirrorCS");var subQ1=sQuery(id+"F0.wireOp",EDGE,"E13.MirrorCS");var subQ2=makeQuery(id+"F0.imprint","INTERSECT",VERTEX,{"derivedFrom":[subQ1,subQ0]});Q8=makeQuery(id+"F0.imprint","IMPRINT",FACE,{"disambiguationData":[TD([[makeQuery(id+"F0.imprint","IMPRINT",EDGE,{"disambiguationData":[TD([[subQ2,-1.0]])],"derivedFrom":subQ1}),-1.0]])]});}
            var Q9;
            {var subQ0=sQuery(id+"F0.wireOp",EDGE,"E44.MirrorCS");var subQ1=sQuery(id+"F0.wireOp",EDGE,"E24.MirrorCS");var subQ2=makeQuery(id+"F0.imprint","INTERSECT",VERTEX,{"derivedFrom":[subQ1,subQ0]});Q9=makeQuery(id+"F0.imprint","IMPRINT",FACE,{"disambiguationData":[TD([[makeQuery(id+"F0.imprint","IMPRINT",EDGE,{"disambiguationData":[TD([[subQ2,-1.0]])],"derivedFrom":subQ1}),1.0]])]});}
            var Q10;
            Q10=makeQuery(id+"F0.imprint","IMPRINT",FACE,{"disambiguationData":[TD([[makeQuery(id+"F0.imprint","IMPRINT",EDGE,{"derivedFrom":sQuery(id+"F0.wireOp",EDGE,"E52.MirrorC")}),1.0]])]});
            var Q11;
            {var subQ7=sQuery(id+"F0.wireOp",EDGE,"E46.MirrorCS");Q11=makeQuery(id+"F0.imprint","IMPRINT",FACE,{"disambiguationData":[TD([[makeQuery(id+"F0.imprint","IMPRINT",EDGE,{"derivedFrom":subQ7}),1.0]])]});}
            var Q12;
            {var subQ5=sQuery(id+"F0.wireOp",EDGE,"E49.MirrorCS");Q12=makeQuery(id+"F0.imprint","IMPRINT",FACE,{"disambiguationData":[TD([[makeQuery(id+"F0.imprint","IMPRINT",EDGE,{"derivedFrom":subQ5}),-1.0]])]});}
            var Q13;
            {var subQ11=sQuery(id+"F0.wireOp",EDGE,"E15");Q13=makeQuery(id+"F0.imprint","IMPRINT",FACE,{"disambiguationData":[TD([[makeQuery(id+"F0.imprint","IMPRINT",EDGE,{"derivedFrom":subQ11}),-1.0]])]});}
            var Q14;
            {var subQ1=sQuery(id+"F0.wireOp",EDGE,"E13.MirrorCS");var subQ10=sQuery(id+"F0.wireOp",EDGE,"E12");var subQ15=makeQuery(id+"F0.imprint","INTERSECT",VERTEX,{"derivedFrom":[subQ10,subQ1]});Q14=makeQuery(id+"F0.imprint","IMPRINT",FACE,{"disambiguationData":[TD([[makeQuery(id+"F0.imprint","IMPRINT",EDGE,{"disambiguationData":[TD([[subQ15,-1.0]])],"derivedFrom":subQ10}),-1.0]])]});}
            var Q15;
            Q15=makeQuery(id+"F0.imprint","IMPRINT",FACE,{"disambiguationData":[TD([[makeQuery(id+"F0.imprint","IMPRINT",EDGE,{"derivedFrom":sQuery(id+"F0.wireOp",EDGE,"E2")}),-1.0]])]});
            extrude(context, id + "F9", {"entities" : qUnion([Q0, Q1, Q2, Q3, Q4, Q5, Q6, Q7, Q8, Q9, Q10, Q11, Q12, Q13, Q14, Q15]), "operationType" : NewBodyOperationType.REMOVE, "depth" : 5 * mm, "offsetDistance" : 25 * mm});
        }
        {
            var Q0;
            {var subQ0=sQuery(id+"F0.wireOp",EDGE,"E59");Q0=makeQuery(id+"F0.imprint","IMPRINT",FACE,{"disambiguationData":[TD([[makeQuery(id+"F0.imprint","IMPRINT",EDGE,{"derivedFrom":subQ0}),-1.0]])]});}
            var Q1;
            {var subQ0=sQuery(id+"F0.wireOp",EDGE,"E8.0");var subQ1=sQuery(id+"F0.wireOp",EDGE,"E0");var subQ2=makeQuery(id+"F0.imprint","INTERSECT",VERTEX,{"disambiguationData":[OD(0.0)],"derivedFrom":[subQ1,subQ0]});Q1=makeQuery(id+"F0.imprint","IMPRINT",FACE,{"disambiguationData":[TD([[makeQuery(id+"F0.imprint","IMPRINT",EDGE,{"disambiguationData":[TD([[subQ2,1.0]])],"derivedFrom":subQ1}),1.0]])]});}
            var Q2;
            {var subQ0=sQuery(id+"F0.wireOp",EDGE,"E8.0");var subQ1=sQuery(id+"F0.wireOp",EDGE,"E0");var subQ2=makeQuery(id+"F0.imprint","INTERSECT",VERTEX,{"disambiguationData":[OD(1.0)],"derivedFrom":[subQ1,subQ0]});Q2=makeQuery(id+"F0.imprint","IMPRINT",FACE,{"disambiguationData":[TD([[makeQuery(id+"F0.imprint","IMPRINT",EDGE,{"disambiguationData":[TD([[subQ2,-1.0]])],"derivedFrom":subQ1}),1.0]])]});}
            var Q3;
            {var subQ0=sQuery(id+"F0.wireOp",EDGE,"E8.0");var subQ1=sQuery(id+"F0.wireOp",EDGE,"E6");var subQ2=makeQuery(id+"F0.imprint","INTERSECT",VERTEX,{"disambiguationData":[OD(0.0)],"derivedFrom":[subQ1,subQ0]});Q3=makeQuery(id+"F0.imprint","IMPRINT",FACE,{"disambiguationData":[TD([[makeQuery(id+"F0.imprint","IMPRINT",EDGE,{"disambiguationData":[TD([[subQ2,1.0]])],"derivedFrom":subQ1}),1.0]])]});}
            var Q4;
            {var subQ4=sQuery(id+"F0.wireOp",EDGE,"E6");var subQ8=makeQuery(id+"F0.imprint","INTERSECT",VERTEX,{"derivedFrom":[subQ4,sQuery(id+"F0.wireOp",EDGE,"E59")]});Q4=makeQuery(id+"F0.imprint","IMPRINT",FACE,{"disambiguationData":[TD([[makeQuery(id+"F0.imprint","IMPRINT",EDGE,{"disambiguationData":[TD([[subQ8,1.0]])],"derivedFrom":subQ4}),1.0]])]});}
            var Q5;
            {var subQ0=sQuery(id+"F0.wireOp",EDGE,"E6");var subQ7=makeQuery(id+"F0.imprint","INTERSECT",VERTEX,{"derivedFrom":[subQ0,sQuery(id+"F0.wireOp",EDGE,"E72.MirrorCS")]});Q5=makeQuery(id+"F0.imprint","IMPRINT",FACE,{"disambiguationData":[TD([[makeQuery(id+"F0.imprint","IMPRINT",EDGE,{"disambiguationData":[TD([[subQ7,1.0]])],"derivedFrom":subQ0}),1.0]])]});}
            var Q6;
            {var subQ0=sQuery(id+"F0.wireOp",EDGE,"E8.0");var subQ1=sQuery(id+"F0.wireOp",EDGE,"E6");var subQ2=makeQuery(id+"F0.imprint","INTERSECT",VERTEX,{"disambiguationData":[OD(1.0)],"derivedFrom":[subQ1,subQ0]});Q6=makeQuery(id+"F0.imprint","IMPRINT",FACE,{"disambiguationData":[TD([[makeQuery(id+"F0.imprint","IMPRINT",EDGE,{"disambiguationData":[TD([[subQ2,-1.0]])],"derivedFrom":subQ1}),1.0]])]});}
            var Q7;
            {var subQ0=sQuery(id+"F0.wireOp",EDGE,"E20.MirrorC");var subQ1=sQuery(id+"F0.wireOp",EDGE,"E8.0");var subQ2=makeQuery(id+"F0.imprint","INTERSECT",VERTEX,{"disambiguationData":[OD(1.0)],"derivedFrom":[subQ1,subQ0]});Q7=makeQuery(id+"F0.imprint","IMPRINT",FACE,{"disambiguationData":[TD([[makeQuery(id+"F0.imprint","IMPRINT",EDGE,{"disambiguationData":[TD([[subQ2,-1.0]])],"derivedFrom":subQ1}),1.0]])]});}
            var Q8;
            {var subQ0=sQuery(id+"F0.wireOp",EDGE,"E21.MirrorC");var subQ1=sQuery(id+"F0.wireOp",EDGE,"E8.0");var subQ2=makeQuery(id+"F0.imprint","INTERSECT",VERTEX,{"disambiguationData":[OD(0.0)],"derivedFrom":[subQ1,subQ0]});Q8=makeQuery(id+"F0.imprint","IMPRINT",FACE,{"disambiguationData":[TD([[makeQuery(id+"F0.imprint","IMPRINT",EDGE,{"disambiguationData":[TD([[subQ2,-1.0]])],"derivedFrom":subQ1}),1.0]])]});}
            var Q9;
            {var subQ0=sQuery(id+"F0.wireOp",EDGE,"E22.MirrorC");var subQ1=sQuery(id+"F0.wireOp",EDGE,"E8.0");var subQ2=makeQuery(id+"F0.imprint","INTERSECT",VERTEX,{"disambiguationData":[OD(0.0)],"derivedFrom":[subQ1,subQ0]});Q9=makeQuery(id+"F0.imprint","IMPRINT",FACE,{"disambiguationData":[TD([[makeQuery(id+"F0.imprint","IMPRINT",EDGE,{"disambiguationData":[TD([[subQ2,-1.0]])],"derivedFrom":subQ1}),1.0]])]});}
            var Q10;
            {var subQ0=sQuery(id+"F0.wireOp",EDGE,"E21.MirrorC");var subQ2=sQuery(id+"F0.wireOp",EDGE,"E8.0");var subQ7=makeQuery(id+"F0.imprint","INTERSECT",VERTEX,{"disambiguationData":[OD(0.0)],"derivedFrom":[subQ2,subQ0]});Q10=makeQuery(id+"F0.imprint","IMPRINT",FACE,{"disambiguationData":[TD([[makeQuery(id+"F0.imprint","IMPRINT",EDGE,{"disambiguationData":[TD([[subQ7,-1.0]])],"derivedFrom":subQ2}),-1.0]])]});}
            var Q11;
            {var subQ1=sQuery(id+"F0.wireOp",EDGE,"E9.0");var subQ4=sQuery(id+"F0.wireOp",EDGE,"E21.MirrorC");var subQ7=makeQuery(id+"F0.imprint","INTERSECT",VERTEX,{"disambiguationData":[OD(0.0)],"derivedFrom":[subQ1,subQ4]});Q11=makeQuery(id+"F0.imprint","IMPRINT",FACE,{"disambiguationData":[TD([[makeQuery(id+"F0.imprint","IMPRINT",EDGE,{"disambiguationData":[TD([[subQ7,-1.0]])],"derivedFrom":subQ1}),1.0]])]});}
            var Q12;
            {var subQ0=sQuery(id+"F0.wireOp",EDGE,"E67");Q12=makeQuery(id+"F0.imprint","IMPRINT",FACE,{"disambiguationData":[TD([[makeQuery(id+"F0.imprint","IMPRINT",EDGE,{"derivedFrom":subQ0}),1.0]])]});}
            var Q13;
            {var subQ0=sQuery(id+"F0.wireOp",EDGE,"E21.MirrorC");var subQ1=sQuery(id+"F0.wireOp",EDGE,"E8.0");var subQ2=makeQuery(id+"F0.imprint","INTERSECT",VERTEX,{"disambiguationData":[OD(1.0)],"derivedFrom":[subQ1,subQ0]});Q13=makeQuery(id+"F0.imprint","IMPRINT",FACE,{"disambiguationData":[TD([[makeQuery(id+"F0.imprint","IMPRINT",EDGE,{"disambiguationData":[TD([[subQ2,-1.0]])],"derivedFrom":subQ1}),1.0]])]});}
            var Q14;
            {var subQ0=sQuery(id+"F0.wireOp",EDGE,"E63.MirrorCS");Q14=makeQuery(id+"F0.imprint","IMPRINT",FACE,{"disambiguationData":[TD([[makeQuery(id+"F0.imprint","IMPRINT",EDGE,{"derivedFrom":subQ0}),1.0]])]});}
            var Q15;
            {var subQ0=sQuery(id+"F0.wireOp",EDGE,"E35.MirrorC");var subQ2=sQuery(id+"F0.wireOp",EDGE,"E9.0");var subQ7=makeQuery(id+"F0.imprint","INTERSECT",VERTEX,{"disambiguationData":[OD(0.0)],"derivedFrom":[subQ2,subQ0]});Q15=makeQuery(id+"F0.imprint","IMPRINT",FACE,{"disambiguationData":[TD([[makeQuery(id+"F0.imprint","IMPRINT",EDGE,{"disambiguationData":[TD([[subQ7,-1.0]])],"derivedFrom":subQ2}),1.0]])]});}
            var Q16;
            {var subQ0=sQuery(id+"F0.wireOp",EDGE,"E34.MirrorC");var subQ1=sQuery(id+"F0.wireOp",EDGE,"E8.0");var subQ2=makeQuery(id+"F0.imprint","INTERSECT",VERTEX,{"disambiguationData":[OD(1.0)],"derivedFrom":[subQ1,subQ0]});Q16=makeQuery(id+"F0.imprint","IMPRINT",FACE,{"disambiguationData":[TD([[makeQuery(id+"F0.imprint","IMPRINT",EDGE,{"disambiguationData":[TD([[subQ2,-1.0]])],"derivedFrom":subQ1}),1.0]])]});}
            var Q17;
            {var subQ1=sQuery(id+"F0.wireOp",EDGE,"E8.0");var subQ4=sQuery(id+"F0.wireOp",EDGE,"E35.MirrorC");var subQ7=makeQuery(id+"F0.imprint","INTERSECT",VERTEX,{"disambiguationData":[OD(0.0)],"derivedFrom":[subQ1,subQ4]});Q17=makeQuery(id+"F0.imprint","IMPRINT",FACE,{"disambiguationData":[TD([[makeQuery(id+"F0.imprint","IMPRINT",EDGE,{"disambiguationData":[TD([[subQ7,-1.0]])],"derivedFrom":subQ1}),-1.0]])]});}
            var Q18;
            {var subQ0=sQuery(id+"F0.wireOp",EDGE,"E35.MirrorC");var subQ1=sQuery(id+"F0.wireOp",EDGE,"E8.0");var subQ2=makeQuery(id+"F0.imprint","INTERSECT",VERTEX,{"disambiguationData":[OD(0.0)],"derivedFrom":[subQ1,subQ0]});Q18=makeQuery(id+"F0.imprint","IMPRINT",FACE,{"disambiguationData":[TD([[makeQuery(id+"F0.imprint","IMPRINT",EDGE,{"disambiguationData":[TD([[subQ2,-1.0]])],"derivedFrom":subQ1}),1.0]])]});}
            var Q19;
            {var subQ0=sQuery(id+"F0.wireOp",EDGE,"E33.MirrorC");var subQ1=sQuery(id+"F0.wireOp",EDGE,"E8.0");var subQ2=makeQuery(id+"F0.imprint","INTERSECT",VERTEX,{"disambiguationData":[OD(0.0)],"derivedFrom":[subQ1,subQ0]});Q19=makeQuery(id+"F0.imprint","IMPRINT",FACE,{"disambiguationData":[TD([[makeQuery(id+"F0.imprint","IMPRINT",EDGE,{"disambiguationData":[TD([[subQ2,-1.0]])],"derivedFrom":subQ1}),1.0]])]});}
            var Q20;
            {var subQ0=sQuery(id+"F0.wireOp",EDGE,"E69.MirrorCS");Q20=makeQuery(id+"F0.imprint","IMPRINT",FACE,{"disambiguationData":[TD([[makeQuery(id+"F0.imprint","IMPRINT",EDGE,{"derivedFrom":subQ0}),1.0]])]});}
            var Q21;
            {var subQ0=sQuery(id+"F0.wireOp",EDGE,"E35.MirrorC");var subQ1=sQuery(id+"F0.wireOp",EDGE,"E8.0");var subQ2=makeQuery(id+"F0.imprint","INTERSECT",VERTEX,{"disambiguationData":[OD(1.0)],"derivedFrom":[subQ1,subQ0]});Q21=makeQuery(id+"F0.imprint","IMPRINT",FACE,{"disambiguationData":[TD([[makeQuery(id+"F0.imprint","IMPRINT",EDGE,{"disambiguationData":[TD([[subQ2,-1.0]])],"derivedFrom":subQ1}),1.0]])]});}
            var Q22;
            {var subQ0=sQuery(id+"F0.wireOp",EDGE,"E65.MirrorCS");Q22=makeQuery(id+"F0.imprint","IMPRINT",FACE,{"disambiguationData":[TD([[makeQuery(id+"F0.imprint","IMPRINT",EDGE,{"derivedFrom":subQ0}),-1.0]])]});}
            var Q23;
            {var subQ0=sQuery(id+"F0.wireOp",EDGE,"E10.MirrorC");var subQ1=sQuery(id+"F0.wireOp",EDGE,"E8.0");var subQ2=makeQuery(id+"F0.imprint","INTERSECT",VERTEX,{"disambiguationData":[OD(0.0)],"derivedFrom":[subQ1,subQ0]});Q23=makeQuery(id+"F0.imprint","IMPRINT",FACE,{"disambiguationData":[TD([[makeQuery(id+"F0.imprint","IMPRINT",EDGE,{"disambiguationData":[TD([[subQ2,-1.0]])],"derivedFrom":subQ1}),1.0]])]});}
            var Q24;
            {var subQ0=sQuery(id+"F0.wireOp",EDGE,"E10.MirrorC");var subQ3=sQuery(id+"F0.wireOp",EDGE,"E9.0");var subQ4=makeQuery(id+"F0.imprint","INTERSECT",VERTEX,{"disambiguationData":[OD(0.0)],"derivedFrom":[subQ3,subQ0]});Q24=makeQuery(id+"F0.imprint","IMPRINT",FACE,{"disambiguationData":[TD([[makeQuery(id+"F0.imprint","IMPRINT",EDGE,{"disambiguationData":[TD([[subQ4,-1.0]])],"derivedFrom":subQ3}),1.0]])]});}
            var Q25;
            {var subQ0=sQuery(id+"F0.wireOp",EDGE,"E10.MirrorC");var subQ3=sQuery(id+"F0.wireOp",EDGE,"E8.0");var subQ7=makeQuery(id+"F0.imprint","INTERSECT",VERTEX,{"disambiguationData":[OD(0.0)],"derivedFrom":[subQ3,subQ0]});Q25=makeQuery(id+"F0.imprint","IMPRINT",FACE,{"disambiguationData":[TD([[makeQuery(id+"F0.imprint","IMPRINT",EDGE,{"disambiguationData":[TD([[subQ7,-1.0]])],"derivedFrom":subQ3}),-1.0]])]});}
            var Q26;
            {var subQ0=sQuery(id+"F0.wireOp",EDGE,"E11.MirrorC");var subQ1=sQuery(id+"F0.wireOp",EDGE,"E8.0");var subQ2=makeQuery(id+"F0.imprint","INTERSECT",VERTEX,{"disambiguationData":[OD(1.0)],"derivedFrom":[subQ1,subQ0]});Q26=makeQuery(id+"F0.imprint","IMPRINT",FACE,{"disambiguationData":[TD([[makeQuery(id+"F0.imprint","IMPRINT",EDGE,{"disambiguationData":[TD([[subQ2,-1.0]])],"derivedFrom":subQ1}),1.0]])]});}
            var Q27;
            {var subQ0=sQuery(id+"F0.wireOp",EDGE,"E73.MirrorCS");Q27=makeQuery(id+"F0.imprint","IMPRINT",FACE,{"disambiguationData":[TD([[makeQuery(id+"F0.imprint","IMPRINT",EDGE,{"derivedFrom":subQ0}),-1.0]])]});}
            var Q28;
            {var subQ0=sQuery(id+"F0.wireOp",EDGE,"E9.0");var subQ1=sQuery(id+"F0.wireOp",EDGE,"E1");var subQ2=makeQuery(id+"F0.imprint","INTERSECT",VERTEX,{"disambiguationData":[OD(0.0)],"derivedFrom":[subQ1,subQ0]});Q28=makeQuery(id+"F0.imprint","IMPRINT",FACE,{"disambiguationData":[TD([[makeQuery(id+"F0.imprint","IMPRINT",EDGE,{"disambiguationData":[TD([[subQ2,-1.0]])],"derivedFrom":subQ1}),1.0]])]});}
            var Q29;
            {var subQ0=sQuery(id+"F0.wireOp",EDGE,"E8.0");var subQ1=sQuery(id+"F0.wireOp",EDGE,"E1");var subQ2=makeQuery(id+"F0.imprint","INTERSECT",VERTEX,{"disambiguationData":[OD(1.0)],"derivedFrom":[subQ1,subQ0]});Q29=makeQuery(id+"F0.imprint","IMPRINT",FACE,{"disambiguationData":[TD([[makeQuery(id+"F0.imprint","IMPRINT",EDGE,{"disambiguationData":[TD([[subQ2,-1.0]])],"derivedFrom":subQ1}),1.0]])]});}
            var Q30;
            {var subQ0=sQuery(id+"F0.wireOp",EDGE,"E61.MirrorCS");Q30=makeQuery(id+"F0.imprint","IMPRINT",FACE,{"disambiguationData":[TD([[makeQuery(id+"F0.imprint","IMPRINT",EDGE,{"derivedFrom":subQ0}),1.0]])]});}
            var Q31;
            {var subQ5=sQuery(id+"F0.wireOp",EDGE,"E87.MirrorCS");Q31=makeQuery(id+"F0.imprint","IMPRINT",FACE,{"disambiguationData":[TD([[makeQuery(id+"F0.imprint","IMPRINT",EDGE,{"derivedFrom":subQ5}),1.0]])]});}
            var Q32;
            {var subQ5=sQuery(id+"F0.wireOp",EDGE,"E86.MirrorCS");Q32=makeQuery(id+"F0.imprint","IMPRINT",FACE,{"disambiguationData":[TD([[makeQuery(id+"F0.imprint","IMPRINT",EDGE,{"derivedFrom":subQ5}),-1.0]])]});}
            var Q33;
            {var subQ3=sQuery(id+"F0.wireOp",EDGE,"E85.MirrorCS");Q33=makeQuery(id+"F0.imprint","IMPRINT",FACE,{"disambiguationData":[TD([[makeQuery(id+"F0.imprint","IMPRINT",EDGE,{"derivedFrom":subQ3}),1.0]])]});}
            var Q34;
            {var subQ4=sQuery(id+"F0.wireOp",EDGE,"E84.MirrorCS");Q34=makeQuery(id+"F0.imprint","IMPRINT",FACE,{"disambiguationData":[TD([[makeQuery(id+"F0.imprint","IMPRINT",EDGE,{"derivedFrom":subQ4}),-1.0]])]});}
            var Q35;
            {var subQ5=sQuery(id+"F0.wireOp",EDGE,"E82.MirrorCS");Q35=makeQuery(id+"F0.imprint","IMPRINT",FACE,{"disambiguationData":[TD([[makeQuery(id+"F0.imprint","IMPRINT",EDGE,{"derivedFrom":subQ5}),1.0]])]});}
            var Q36;
            {var subQ5=sQuery(id+"F0.wireOp",EDGE,"E83.MirrorCS");Q36=makeQuery(id+"F0.imprint","IMPRINT",FACE,{"disambiguationData":[TD([[makeQuery(id+"F0.imprint","IMPRINT",EDGE,{"derivedFrom":subQ5}),-1.0]])]});}
            var Q37;
            {var subQ0=sQuery(id+"F0.wireOp",EDGE,"E71.MirrorCS");Q37=makeQuery(id+"F0.imprint","IMPRINT",FACE,{"disambiguationData":[TD([[makeQuery(id+"F0.imprint","IMPRINT",EDGE,{"derivedFrom":subQ0}),-1.0]])]});}
            var Q38;
            {var subQ0=sQuery(id+"F0.wireOp",EDGE,"E80");Q38=makeQuery(id+"F0.imprint","IMPRINT",FACE,{"disambiguationData":[TD([[makeQuery(id+"F0.imprint","IMPRINT",EDGE,{"derivedFrom":subQ0}),-1.0]])]});}
            var Q39;
            {var subQ0=sQuery(id+"F0.wireOp",EDGE,"E81");Q39=makeQuery(id+"F0.imprint","IMPRINT",FACE,{"disambiguationData":[TD([[makeQuery(id+"F0.imprint","IMPRINT",EDGE,{"derivedFrom":subQ0}),1.0]])]});}
            extrude(context, id + "F10", {"entities" : qUnion([Q0, Q1, Q2, Q3, Q4, Q5, Q6, Q7, Q8, Q9, Q10, Q11, Q12, Q13, Q14, Q15, Q16, Q17, Q18, Q19, Q20, Q21, Q22, Q23, Q24, Q25, Q26, Q27, Q28, Q29, Q30, Q31, Q32, Q33, Q34, Q35, Q36, Q37, Q38, Q39]), "depth" : 1 * mm, "offsetDistance" : 25 * mm});
        }
        {
            var Q0;
            Q0=makeQuery(id+"F6.opExtrude","CAP_EDGE",EDGE,{"disambiguationData":[OSD([sQuery(id+"F0.wireOp",EDGE,"E13.MirrorCS")])],"isStart":false});
            chamfer(context, id + "F11", {"entities" : qUnion([Q0]), "width" : 7 * mm, "tangentPropagation" : true});
        }
        {
            var Q0;
            Q0=makeQuery(id+"F6.opExtrude","CAP_EDGE",EDGE,{"disambiguationData":[OSD([sQuery(id+"F0.wireOp",EDGE,"E12")])],"isStart":false});
            chamfer(context, id + "F12", {"entities" : qUnion([Q0]), "width" : 7 * mm, "tangentPropagation" : true});
        }
        {
            var Q0;
            Q0=makeQuery(id+"F6.opExtrude","CAP_EDGE",EDGE,{"disambiguationData":[OSD([sQuery(id+"F0.wireOp",EDGE,"E31.MirrorCS")])],"isStart":false});
            chamfer(context, id + "F13", {"entities" : qUnion([Q0]), "width" : 7 * mm, "tangentPropagation" : true});
        }
        {
            var Q0;
            Q0=makeQuery(id+"F6.opExtrude","CAP_EDGE",EDGE,{"disambiguationData":[OSD([sQuery(id+"F0.wireOp",EDGE,"E24.MirrorCS")])],"isStart":false});
            chamfer(context, id + "F14", {"entities" : qUnion([Q0]), "width" : 7 * mm, "tangentPropagation" : true});
        }
    });
